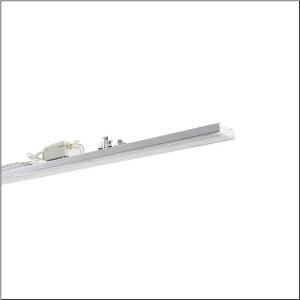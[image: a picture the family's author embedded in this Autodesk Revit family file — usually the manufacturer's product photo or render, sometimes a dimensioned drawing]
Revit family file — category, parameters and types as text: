
# Revit family: licross_11_recessed_mo_51tl10dv4e5g
name_source: partatom
category: Lighting Fixtures
units: mm (PartAtom-declared; Revit-internal decimal feet)

## family parameters
Cut with Voids When Loaded = No
Host = Face
Light Source = No
Part Type = Normal
Room Calculation Point = No
Round Connector Dimension = Use Diameter
Shared = No

## types (1)
- --- (1 x LED, 14930 lm, 84.1 W, 4000K)
    Apparent Load = 84 VA
    CIE Flux Codes = 50 81 96 100 100
    Color Rendering = 80
    Color Temperature = 4000K
    Default Elevation = 1800 mm
    Description = Licross 11 Recessed MO, luminaire insert, of sheet steel, coil coated, white, length: 2.250mm, width: 66mm, height: 67mm, LED rated luminous flux: 14.930lm, light colour: 840, SDCM (Standard Deviation of Colour Matching)MacAdam ≤ 2 SDCM (initial), control gear: DALI 2, with plug, 5-pole, with phase selection, mains connection: 220..240V, AC, 50/60Hz, rated input power: 84W, internal wiring halogen-free, primary optical cover: cover, of PMMA, light emission: direct distribution, primary light characteristic: symmetric, protection rating (complete): IP40, insulation class (complete): insulation class I (protective earthing), certification: CE, ENEC, VDE, UKCA, protection symbol: D if used in an environment without relevant dust loads with corresponding accessories, impact resistance: IK06, permissible ambient temperature for indoor applications: -25..+35°C, corresponds to IFS (International Featured Standards) requirements for safety and quality in the food industry, reducing of maximum allowable ambient temperature of 5°C with ceiling mounting, LABS conformity tested according to VDMA 24364:2018-05, The light source and the operating device comply with the requirements of the Ecodesign Regulation (EU) 2019/2020 and are replaceable in accordance with this regulation, packaging unit: 1 piece
    Height = 58 mm
    Lamp = 1 x LED
    Lamp Light Flux = 14930 lm
    Lamp Power = 84.1 W
    Lamp count = 1
    Length = 2250 mm
    Luminous efficacy = 178 lm/W
    Manufacturer = Siteco
    ModVariant = No
    Model = 51TL10DV4E5G
    Mounting Place = Ceiling
    Mounting Type = Pendant
    Number of Poles = 1
    OnlyDefault = Yes
    Power Factor = 1
    Product Name = Licross 11 Recessed MO
    Product group = luminaire insert | ceiling pendant
    ProductGroupID = 901
    Protection Class = Protection class I
    Protection Degree = IP 40
    RLX_Detail_Level = 1
    RLX_Emergency_Light_Flux = 0 lm
    RLX_Emergency_Type = 0
    RLX_Emergency_Type_DB = No
    RlxData = <blob elided: 29397 chars, md5=c8eb7f08>
    Socket = socket
    Standby Power = 0 W
    System Light Flux = 14930 lm
    System Power = 84 W
    Type Comments = factory setting: luminous flux: 100 % | dim-lin: 254 | 378 mA
    Type Image = l_1296930.jpg
    URL = http://relux.com
    VarID = @adj_102911
    Voltage = 0 V
    Weight = 0.00 kg
    Width = 66 mm

## geometry (parser evidence)
native form markers: Blend x4, Sweep x10
no freeform markers — native parametric forms only
